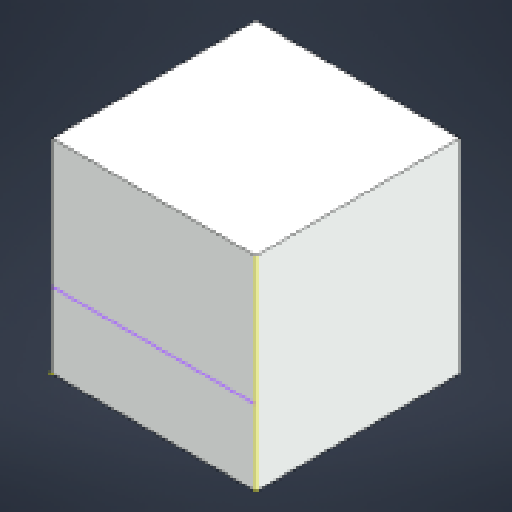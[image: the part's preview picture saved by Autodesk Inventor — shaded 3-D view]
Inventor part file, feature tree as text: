
AUTODESK INVENTOR PART (.ipt)
format: ipt  version: 2023.1 (Build 271208000, 208)  size: 133,120 bytes
history: native  units: in
note: dims shown in document units (in); Inventor stores cm internally (conversion verified against a paired STEP export)
features: sketch x2, extrude x1
ambient origin geometry x8: Origin, YZ Plane, XZ Plane, XY Plane, X Axis, Y Axis, Z Axis, Center Point
bodies: Solid1 (feature_tree)
feature tree (3):
  extrude  "Extrusion1"  Depth=20.0in
  sketch  "Sketch3"  dims[d5=20.0in d6=0.0in]
  sketch  "Sketch2"  dims[d3=20.0in d4=20.0in]
